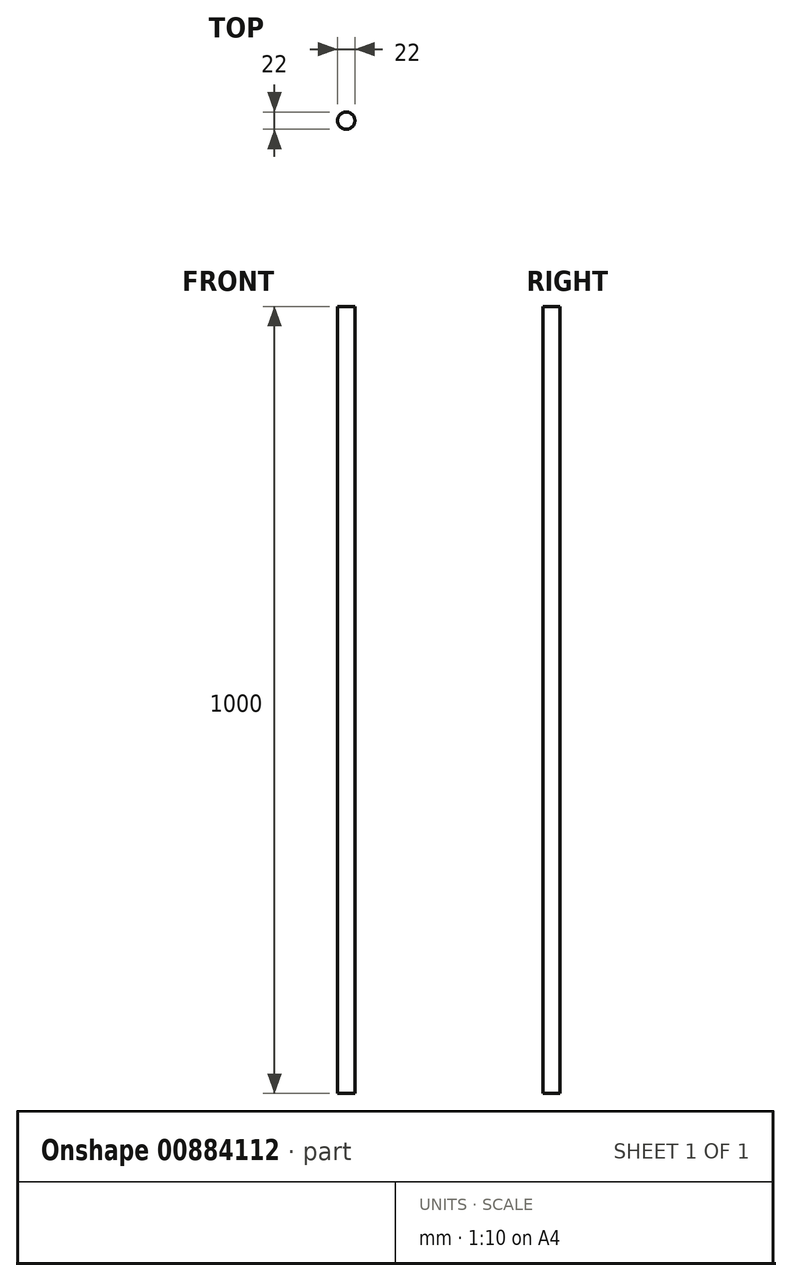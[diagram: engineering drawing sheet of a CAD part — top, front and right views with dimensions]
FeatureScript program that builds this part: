
annotation { "Feature Type Name" : "Feature", "Feature Type Description" : "" }
export const myFeature = defineFeature(function(context is Context, id is Id, definition is map)
    precondition{}
    {
        {
            var Q0;
            Q0=qCreatedBy(makeId("Top.planeOp"),FACE);
            var sketch = newSketch(context, id + "F0", { "sketchPlane" : qUnion([Q0])});
            skCircle(sketch, "E0", {"center": v(0, 0) * mm, "radius": 11 * mm});
            skSolve(sketch);
        }
        {
            var Q0;
            Q0=qSketchRegion(id+"F0",true);
            extrude(context, id + "F1", {"entities" : qUnion([Q0]), "depth" : 1000 * mm, "offsetDistance" : 25 * mm});
        }
    });
